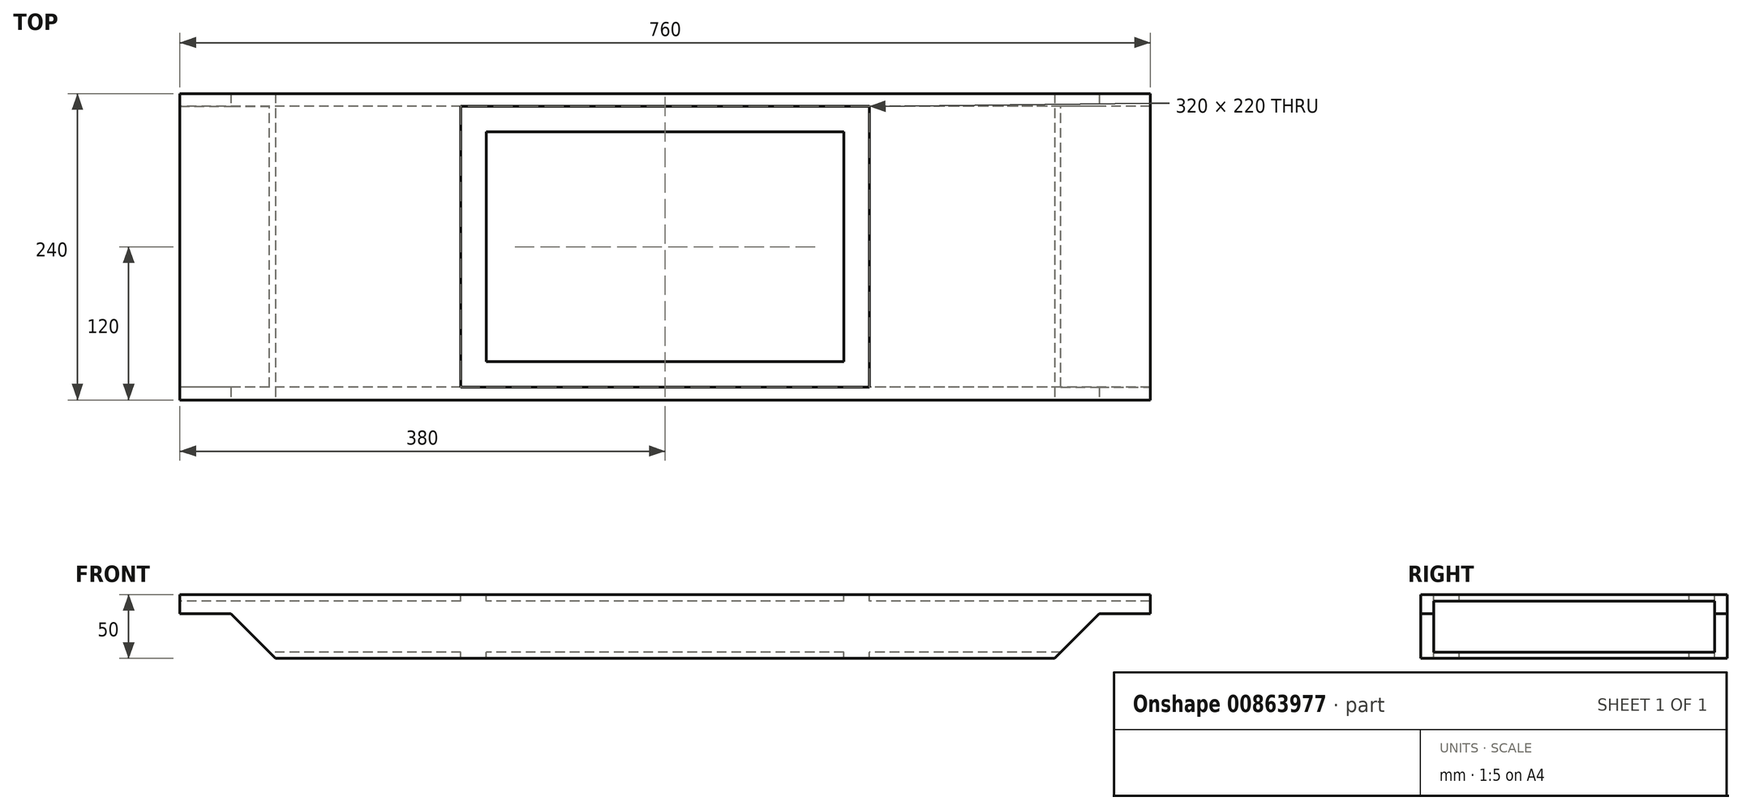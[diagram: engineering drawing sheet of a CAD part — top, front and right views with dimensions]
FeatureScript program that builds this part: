
annotation { "Feature Type Name" : "Feature", "Feature Type Description" : "" }
export const myFeature = defineFeature(function(context is Context, id is Id, definition is map)
    precondition{}
    {
        {
            var Q0;
            Q0=qCreatedBy(makeId("Top.planeOp"),FACE);
            var sketch = newSketch(context, id + "F0", { "sketchPlane" : qUnion([Q0])});
            skLineSegment(sketch, "E0", {"start": v(-380, 120) * mm, "end": v(-380, -120) * mm});
            skLineSegment(sketch, "E1", {"start": v(380, 120) * mm, "end": v(380, -120) * mm});
            skLineSegment(sketch, "E2", {"start": v(380, -120) * mm, "end": v(-380, -120) * mm});
            skLineSegment(sketch, "E3", {"start": v(-380, 120) * mm, "end": v(380, 120) * mm});
            skSolve(sketch);
        }
        {
            var Q0;
            Q0=makeQuery(id+"F0.imprint","IMPRINT",FACE,{"disambiguationData":[TD([[makeQuery(id+"F0.imprint","IMPRINT",EDGE,{"derivedFrom":sQuery(id+"F0.wireOp",EDGE,"E0")}),1.0]])]});
            extrude(context, id + "F1", {"entities" : qUnion([Q0]), "depth" : 50 * mm, "offsetDistance" : 25 * mm});
        }
        {
            var Q0;
            Q0=makeQuery(id+"F1.opExtrude","SWEPT_FACE",FACE,{"disambiguationData":[OSD([sQuery(id+"F0.wireOp",EDGE,"E2")])]});
            var sketch = newSketch(context, id + "F2", { "sketchPlane" : qUnion([Q0])});
            skLineSegment(sketch, "E4", {"start": v(-380, 35) * mm, "end": v(-340, 35) * mm});
            skLineSegment(sketch, "E5", {"start": v(-340, 35) * mm, "end": v(-305, 0) * mm});
            skLineSegment(sketch, "E6", {"start": v(-380, 35) * mm, "end": v(-380, 0) * mm});
            skLineSegment(sketch, "E7", {"start": v(-380, 0) * mm, "end": v(-305, 0) * mm});
            skLineSegment(sketch, "E8.MirrorCS", {"start": v(380, 0) * mm, "end": v(305, 0) * mm});
            skLineSegment(sketch, "E9.MirrorCS", {"start": v(380, 35) * mm, "end": v(380, 0) * mm});
            skLineSegment(sketch, "E10.MirrorCS", {"start": v(380, 35) * mm, "end": v(340, 35) * mm});
            skLineSegment(sketch, "E11.MirrorCS", {"start": v(340, 35) * mm, "end": v(305, 0) * mm});
            skSolve(sketch);
        }
        {
            var Q0;
            Q0=makeQuery(id+"F1.opExtrude","SWEPT_FACE",FACE,{"disambiguationData":[OSD([sQuery(id+"F0.wireOp",EDGE,"E0")])]});
            var sketch = newSketch(context, id + "F3", { "sketchPlane" : qUnion([Q0])});
            skLineSegment(sketch, "E12.0", {"start": v(-110, 45) * mm, "end": v(110, 45) * mm});
            skLineSegment(sketch, "E13.0", {"start": v(-110, 5) * mm, "end": v(110, 5) * mm});
            skLineSegment(sketch, "E14.0", {"start": v(-110, 5) * mm, "end": v(-110, 45) * mm});
            skLineSegment(sketch, "E15.0", {"start": v(110, 45) * mm, "end": v(110, 5) * mm});
            skSolve(sketch);
        }
        {
            var Q0;
            Q0=makeQuery(id+"F3.imprint","IMPRINT",FACE,{"disambiguationData":[TD([[makeQuery(id+"F3.imprint","IMPRINT",EDGE,{"derivedFrom":sQuery(id+"F3.wireOp",EDGE,"E12.0")}),-1.0]])]});
            extrude(context, id + "F4", {"entities" : qUnion([Q0]), "operationType" : NewBodyOperationType.REMOVE, "oppositeDirection" : true, "depth" : 760 * mm, "offsetDistance" : 25 * mm});
        }
        {
            var Q0;
            Q0=makeQuery(id+"F2.imprint","IMPRINT",FACE,{"disambiguationData":[TD([[makeQuery(id+"F2.imprint","IMPRINT",EDGE,{"derivedFrom":sQuery(id+"F2.wireOp",EDGE,"E8.MirrorCS")}),-1.0]])]});
            var Q1;
            Q1=makeQuery(id+"F2.imprint","IMPRINT",FACE,{"disambiguationData":[TD([[makeQuery(id+"F2.imprint","IMPRINT",EDGE,{"derivedFrom":sQuery(id+"F2.wireOp",EDGE,"E4")}),-1.0]])]});
            extrude(context, id + "F5", {"entities" : qUnion([Q0, Q1]), "operationType" : NewBodyOperationType.REMOVE, "oppositeDirection" : true, "depth" : 240 * mm, "offsetDistance" : 25 * mm});
        }
        {
            var Q0;
            Q0=makeQuery(id+"F1.opExtrude","CAP_FACE",FACE,{"disambiguationData":[OSD([sQuery(id+"F0.wireOp",EDGE,"E0"),sQuery(id+"F0.wireOp",EDGE,"E1"),sQuery(id+"F0.wireOp",EDGE,"E2"),sQuery(id+"F0.wireOp",EDGE,"E3")])],"isStart":false});
            var sketch = newSketch(context, id + "F6", { "sketchPlane" : qUnion([Q0])});
            skLineSegment(sketch, "E16", {"start": v(-140, 90) * mm, "end": v(140, 90) * mm});
            skLineSegment(sketch, "E17", {"start": v(140, 90) * mm, "end": v(140, -90) * mm});
            skLineSegment(sketch, "E18", {"start": v(140, -90) * mm, "end": v(-140, -90) * mm});
            skLineSegment(sketch, "E19", {"start": v(-140, -90) * mm, "end": v(-140, 90) * mm});
            skLineSegment(sketch, "E20", {"start": v(160, 110) * mm, "end": v(160, -110) * mm});
            skLineSegment(sketch, "E21", {"start": v(-160, 110) * mm, "end": v(-160, -110) * mm});
            skLineSegment(sketch, "E22", {"start": v(-160, 110) * mm, "end": v(160, 110) * mm});
            skLineSegment(sketch, "E23", {"start": v(160, -110) * mm, "end": v(-160, -110) * mm});
            skSolve(sketch);
        }
        {
            var Q0;
            Q0 = qSketchRegion(id + "F6", true);
            extrude(context, id + "F7", {"entities" : qUnion([Q0]), "operationType" : NewBodyOperationType.REMOVE, "oppositeDirection" : true, "depth" : 50 * mm, "offsetDistance" : 25 * mm});
        }
    });
